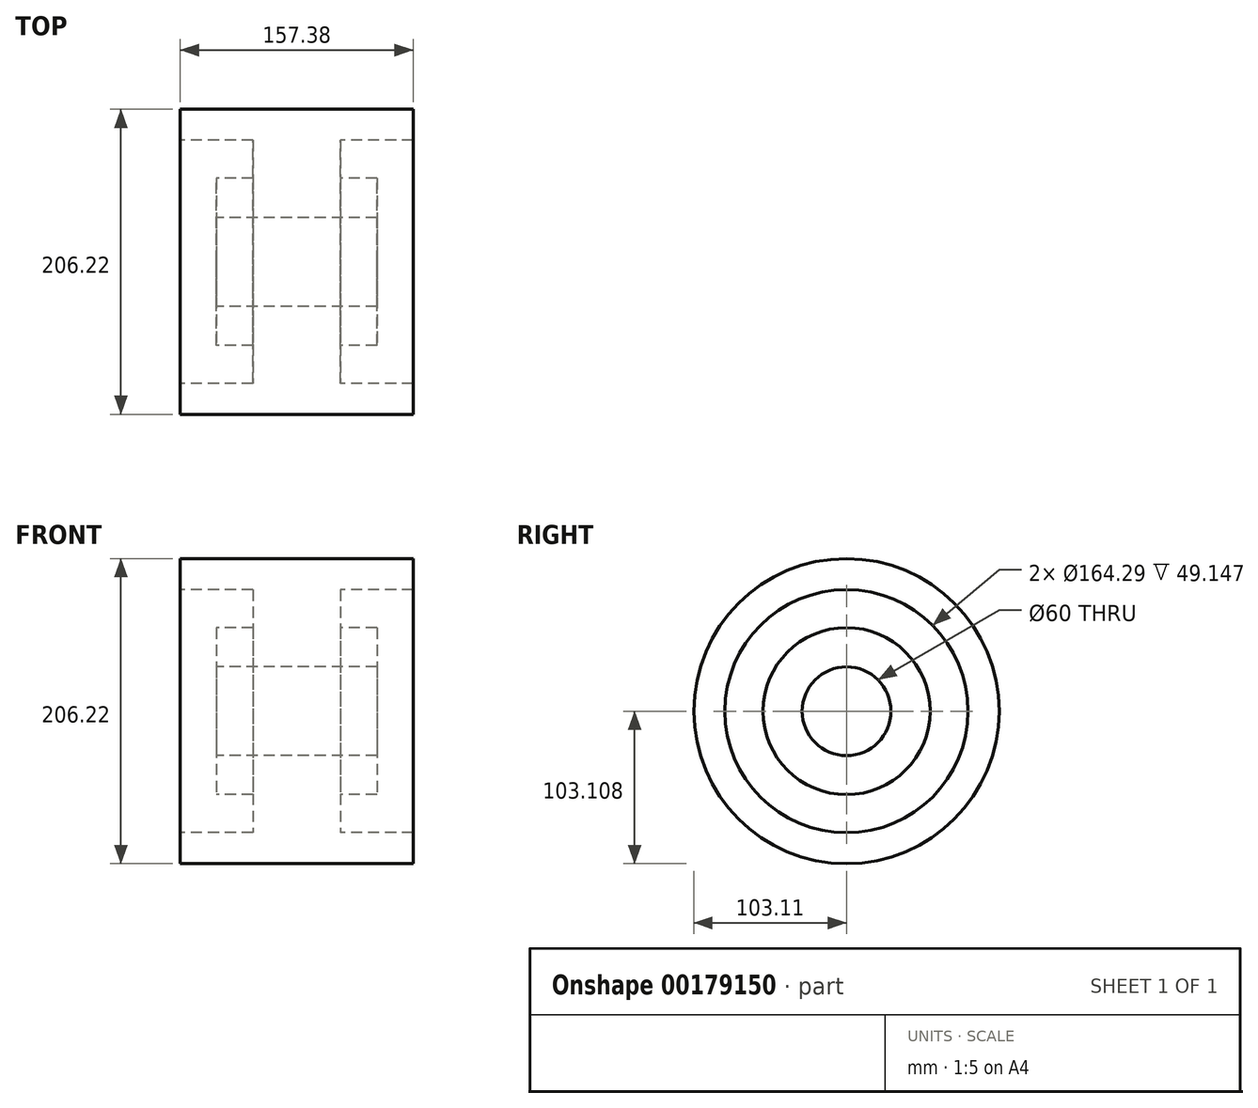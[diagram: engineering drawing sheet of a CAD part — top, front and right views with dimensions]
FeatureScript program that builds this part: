
annotation { "Feature Type Name" : "Feature", "Feature Type Description" : "" }
export const myFeature = defineFeature(function(context is Context, id is Id, definition is map)
    precondition{}
    {
        {
            var Q0;
            Q0=qCreatedBy(makeId("Front.planeOp"),FACE);
            var sketch = newSketch(context, id + "F0", { "sketchPlane" : qUnion([Q0])});
            skLineSegment(sketch, "E0", {"start": v(-96.6, -56.43) * mm, "end": v(96.6, -56.43) * mm, "construction": true});
            skLineSegment(sketch, "E1", {"start": v(0, -56.43) * mm, "end": v(0, 83.08) * mm, "construction": true});
            skPoint(sketch, "E1.startSnap0", {"position": v(0, -56.43) * mm});
            skLineSegment(sketch, "E2", {"start": v(-54.18, 0) * mm, "end": v(-54.18, -26.43) * mm});
            skLineSegment(sketch, "E3", {"start": v(-54.18, -26.43) * mm, "end": v(54.18, -26.43) * mm});
            skLineSegment(sketch, "E4", {"start": v(54.18, -26.43) * mm, "end": v(54.18, 0) * mm});
            skLineSegment(sketch, "E5", {"start": v(54.18, 0) * mm, "end": v(29.54, 0) * mm});
            skLineSegment(sketch, "E6", {"start": v(29.54, 0) * mm, "end": v(29.54, 17.27) * mm});
            skLineSegment(sketch, "E7", {"start": v(29.54, 17.27) * mm, "end": v(29.54, 25.71) * mm});
            skLineSegment(sketch, "E8", {"start": v(29.54, 25.71) * mm, "end": v(78.7, 25.71) * mm});
            skLineSegment(sketch, "E9", {"start": v(78.7, 25.71) * mm, "end": v(78.7, 46.68) * mm});
            skLineSegment(sketch, "E10", {"start": v(78.7, 46.68) * mm, "end": v(-78.7, 46.68) * mm});
            skLineSegment(sketch, "E11", {"start": v(-78.7, 46.68) * mm, "end": v(-78.7, 25.71) * mm});
            skLineSegment(sketch, "E12", {"start": v(-78.7, 25.71) * mm, "end": v(-29.54, 25.71) * mm});
            skLineSegment(sketch, "E13", {"start": v(-29.54, 25.71) * mm, "end": v(-29.54, 0) * mm});
            skLineSegment(sketch, "E14", {"start": v(-29.54, 0) * mm, "end": v(-54.18, 0) * mm});
            skSolve(sketch);
        }
        {
            var Q0;
            Q0=makeQuery(id+"F0.imprint","IMPRINT",FACE,{"disambiguationData":[TD([[makeQuery(id+"F0.imprint","IMPRINT",EDGE,{"derivedFrom":sQuery(id+"F0.wireOp",EDGE,"E2")}),1.0]])]});
            var Q1;
            Q1=sQuery(id+"F0.wireOp",EDGE,"E0");
            revolve(context, id + "F1", {"entities" : qUnion([Q0]), "axis" : qUnion([Q1]), "revolveType" : RevolveType.FULL});
        }
    });
